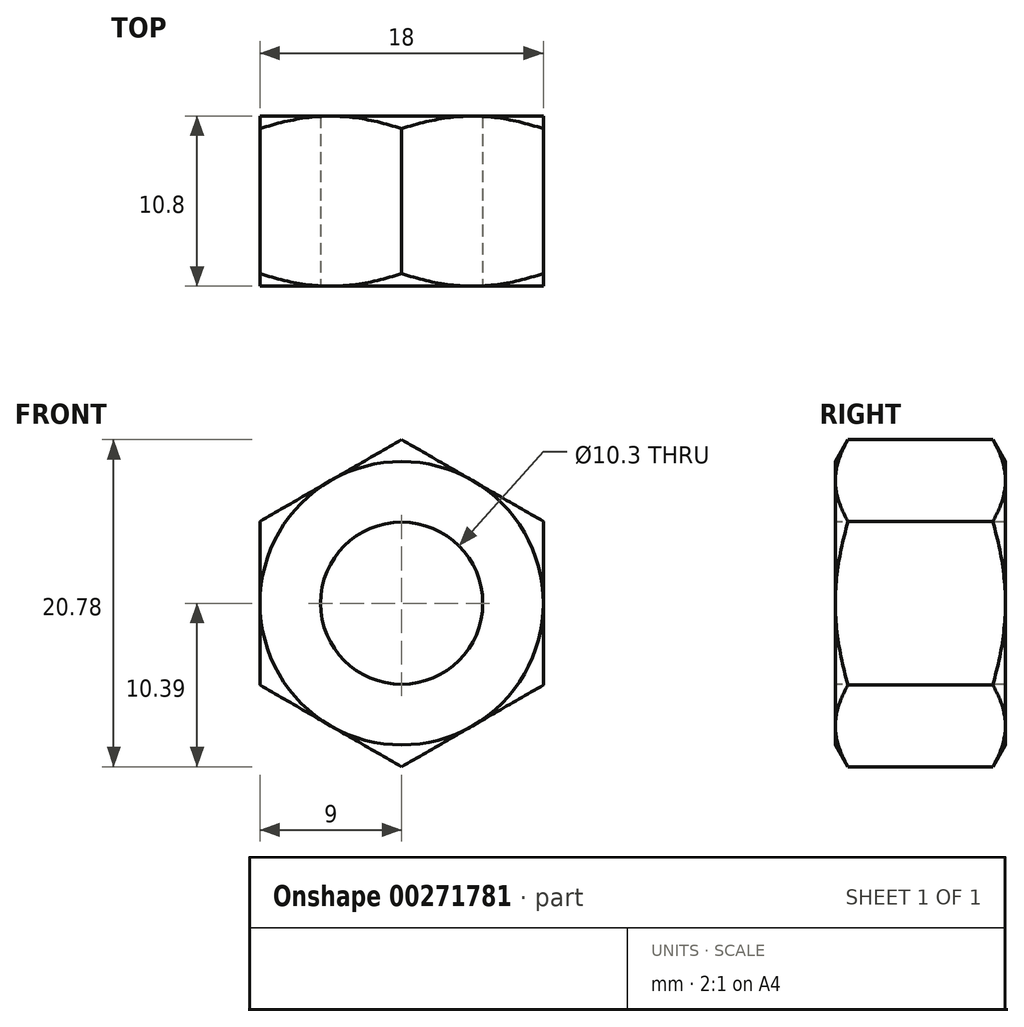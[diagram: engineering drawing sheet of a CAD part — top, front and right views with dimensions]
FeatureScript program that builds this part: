
annotation { "Feature Type Name" : "Feature", "Feature Type Description" : "" }
export const myFeature = defineFeature(function(context is Context, id is Id, definition is map)
    precondition{}
    {
        {
            var Q0;
            Q0=qCreatedBy(makeId("Front.planeOp"),FACE);
            var sketch = newSketch(context, id + "F0", { "sketchPlane" : qUnion([Q0])});
            skCircle(sketch, "E0.cCircle", {"center": v(0, 0) * mm, "radius": 9 * mm, "construction": true});
            skLineSegment(sketch, "E0.0", {"start": v(9, 5.2) * mm, "end": v(9, -5.2) * mm});
            skLineSegment(sketch, "E0.1", {"start": v(9, -5.2) * mm, "end": v(0, -10.4) * mm});
            skLineSegment(sketch, "E0.2", {"start": v(0, -10.4) * mm, "end": v(-9, -5.2) * mm});
            skLineSegment(sketch, "E0.3", {"start": v(-9, -5.2) * mm, "end": v(-9, 5.2) * mm});
            skLineSegment(sketch, "E0.4", {"start": v(-9, 5.2) * mm, "end": v(0, 10.4) * mm});
            skLineSegment(sketch, "E0.5", {"start": v(0, 10.4) * mm, "end": v(9, 5.2) * mm});
            skPoint(sketch, "E0.0.midPoint", {"position": v(9, 0) * mm});
            skSolve(sketch);
        }
        {
            var Q0;
            Q0 = qSketchRegion(id + "F0", true);
            extrude(context, id + "F1", {"entities" : qUnion([Q0]), "oppositeDirection" : true, "depth" : 10.8 * mm});
        }
        {
            var Q0;
            Q0=qCreatedBy(makeId("Right.planeOp"),FACE);
            var sketch = newSketch(context, id + "F2", { "sketchPlane" : qUnion([Q0])});
            skLineSegment(sketch, "E1", {"start": v(-13.45, 0) * mm, "end": v(28.24, 0) * mm, "construction": true});
            skLineSegment(sketch, "E2", {"start": v(0, 9) * mm, "end": v(3.11, 14.4) * mm});
            skLineSegment(sketch, "E3", {"start": v(-4, 14.4) * mm, "end": v(-4, 9) * mm});
            skLineSegment(sketch, "E4", {"start": v(-4, 9) * mm, "end": v(0, 9) * mm});
            skLineSegment(sketch, "E5", {"start": v(3.11, 14.4) * mm, "end": v(-4, 14.4) * mm});
            skLineSegment(sketch, "E6", {"start": v(5.4, 20.22) * mm, "end": v(5.4, 2.58) * mm, "construction": true});
            skLineSegment(sketch, "E7.MirrorCS", {"start": v(10.8, 9) * mm, "end": v(7.69, 14.4) * mm});
            skLineSegment(sketch, "E8.MirrorCS", {"start": v(14.8, 9) * mm, "end": v(10.8, 9) * mm});
            skLineSegment(sketch, "E9.MirrorCS", {"start": v(14.8, 14.4) * mm, "end": v(14.8, 9) * mm});
            skLineSegment(sketch, "E10.MirrorCS", {"start": v(7.69, 14.4) * mm, "end": v(14.8, 14.4) * mm});
            skSolve(sketch);
        }
        {
            var Q0;
            Q0=makeQuery(id+"F2.imprint","IMPRINT",FACE,{"disambiguationData":[TD([[makeQuery(id+"F2.imprint","IMPRINT",EDGE,{"derivedFrom":sQuery(id+"F2.wireOp",EDGE,"E2")}),1.0]])]});
            var Q1;
            Q1=makeQuery(id+"F2.imprint","IMPRINT",FACE,{"disambiguationData":[TD([[makeQuery(id+"F2.imprint","IMPRINT",EDGE,{"derivedFrom":sQuery(id+"F2.wireOp",EDGE,"E7.MirrorCS")}),-1.0]])]});
            var Q2;
            Q2=sQuery(id+"F2.wireOp",EDGE,"E1");
            revolve(context, id + "F3", {"operationType" : NewBodyOperationType.REMOVE, "entities" : qUnion([Q0, Q1]), "axis" : qUnion([Q2]), "revolveType" : RevolveType.FULL, "oppositeDirection" : true});
        }
        {
            var Q0;
            Q0=makeQuery(id+"F1.opExtrude","CAP_FACE",FACE,{"disambiguationData":[OSD([sQuery(id+"F0.wireOp",EDGE,"E0.0"),sQuery(id+"F0.wireOp",EDGE,"E0.1"),sQuery(id+"F0.wireOp",EDGE,"E0.2"),sQuery(id+"F0.wireOp",EDGE,"E0.3"),sQuery(id+"F0.wireOp",EDGE,"E0.4"),sQuery(id+"F0.wireOp",EDGE,"E0.5")])],"isStart":true});
            var sketch = newSketch(context, id + "F4", { "sketchPlane" : qUnion([Q0])});
            skPoint(sketch, "E11", {"position": v(0, 0) * mm});
            skSolve(sketch);
        }
        {
            var Q0;
            Q0=sQuery(id+"F4.wireOp",VERTEX,"E11");
            var Q1;
            Q1=makeQuery(id+"F1.opExtrude","SWEPT_BODY",BODY,{"disambiguationData":[OSD([sQuery(id+"F0.wireOp",EDGE,"E0.0"),sQuery(id+"F0.wireOp",EDGE,"E0.1"),sQuery(id+"F0.wireOp",EDGE,"E0.2"),sQuery(id+"F0.wireOp",EDGE,"E0.3"),sQuery(id+"F0.wireOp",EDGE,"E0.4"),sQuery(id+"F0.wireOp",EDGE,"E0.5")])]});
            hole(context, id + "F5", {"style" : HoleStyle.SIMPLE, "endStyle" : HoleEndStyle.THROUGH, "standardTappedOrClearance" : lookupTablePath({ "standard" : "ISO", "fit" : "Normal", "engagement" : "75%", "pitch" : "1.75 mm", "size" : "M12", "type" : "Tapped" }), "standardBlindInLast" : lookupTablePath({ "fit" : "Standard", "standard" : "ISO", "engagement" : "75%", "pitch" : "1.75 mm", "size" : "M12", "type" : "Tapped" }), "holeDiameter" : 10.3 * mm, "showTappedDepth" : true, "tappedDepth" : 12 * mm, "tapClearance" : 3, "locations" : qUnion([Q0]), "scope" : qUnion([Q1]), "majorDiameter" : 12 * mm});
        }
    });
